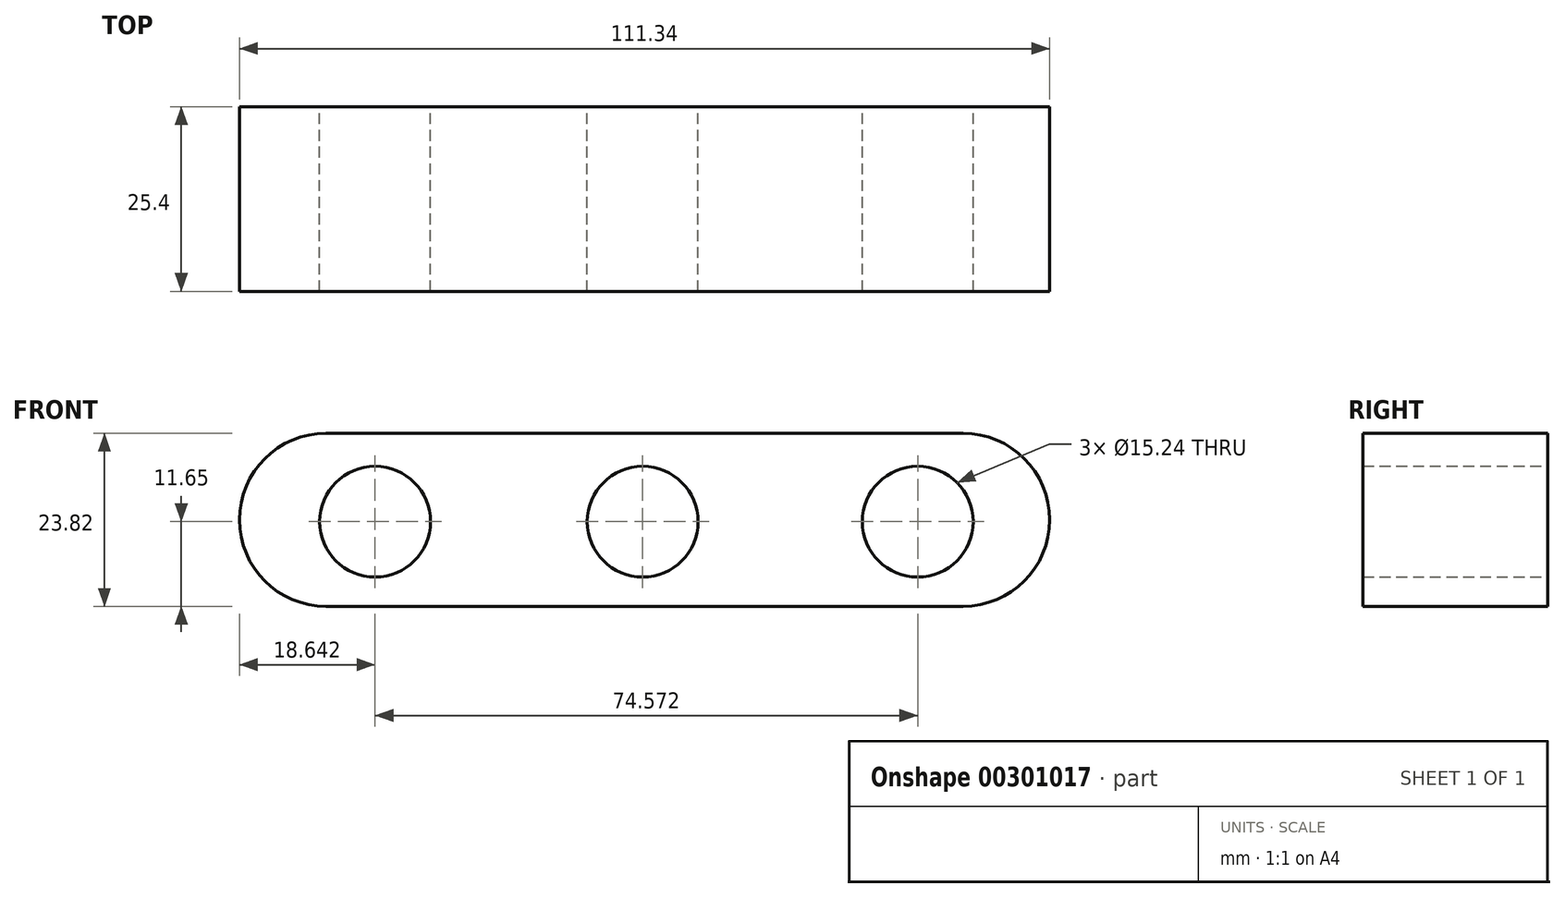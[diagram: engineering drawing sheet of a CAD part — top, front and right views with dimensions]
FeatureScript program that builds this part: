
annotation { "Feature Type Name" : "Feature", "Feature Type Description" : "" }
export const myFeature = defineFeature(function(context is Context, id is Id, definition is map)
    precondition{}
    {
        {
            var Q0;
            Q0=qCreatedBy(makeId("Front.planeOp"),FACE);
            var sketch = newSketch(context, id + "F0", { "sketchPlane" : qUnion([Q0])});
            skLineSegment(sketch, "E0.bottom", {"start": v(-43.5, 12.17) * mm, "end": v(44.02, 12.17) * mm});
            skLineSegment(sketch, "E0.top", {"start": v(-43.5, -11.65) * mm, "end": v(44.02, -11.65) * mm});
            skArc(sketch, "E1", {"start": v(-43.5, 12.17) * mm, "mid": v(-55.41, 0.26) * mm, "end": v(-43.5, -11.65) * mm});
            skArc(sketch, "E2", {"start": v(44.02, -11.65) * mm, "mid": v(55.93, 0.26) * mm, "end": v(44.02, 12.17) * mm});
            skCircle(sketch, "E3", {"center": v(-36.77, 0) * mm, "radius": 9.44 * mm});
            skCircle(sketch, "E4", {"center": v(0, 0) * mm, "radius": 9.44 * mm});
            skCircle(sketch, "E5", {"center": v(37.8, 0) * mm, "radius": 9.44 * mm});
            skSolve(sketch);
        }
        {
            var Q0;
            Q0=makeQuery(id+"F0.imprint","IMPRINT",FACE,{"disambiguationData":[TD([[makeQuery(id+"F0.imprint","IMPRINT",EDGE,{"derivedFrom":sQuery(id+"F0.wireOp",EDGE,"E3")}),1.0]])]});
            var Q1;
            Q1=makeQuery(id+"F0.imprint","IMPRINT",FACE,{"disambiguationData":[TD([[makeQuery(id+"F0.imprint","IMPRINT",EDGE,{"derivedFrom":sQuery(id+"F0.wireOp",EDGE,"E4")}),1.0]])]});
            var Q2;
            Q2=makeQuery(id+"F0.imprint","IMPRINT",FACE,{"disambiguationData":[TD([[makeQuery(id+"F0.imprint","IMPRINT",EDGE,{"derivedFrom":sQuery(id+"F0.wireOp",EDGE,"E5")}),1.0]])]});
            var Q3;
            Q3=makeQuery(id+"F0.imprint","IMPRINT",FACE,{"disambiguationData":[TD([[makeQuery(id+"F0.imprint","IMPRINT",EDGE,{"derivedFrom":sQuery(id+"F0.wireOp",EDGE,"E0.bottom")}),-1.0]])]});
            extrude(context, id + "F1", {"entities" : qUnion([Q0, Q1, Q2, Q3]), "depth" : 25.4 * mm});
        }
        {
            var Q0;
            Q0=sQuery(id+"F0.wireOp",VERTEX,"E3.center");
            var Q1;
            Q1=makeQuery(id+"F1.opExtrude","SWEPT_BODY",BODY,{"disambiguationData":[OSD([sQuery(id+"F0.wireOp",EDGE,"E0.bottom"),sQuery(id+"F0.wireOp",EDGE,"E0.top"),sQuery(id+"F0.wireOp",EDGE,"E1"),sQuery(id+"F0.wireOp",EDGE,"E2")])]});
            hole(context, id + "F2", {"style" : HoleStyle.SIMPLE, "endStyle" : HoleEndStyle.THROUGH, "oppositeDirection" : true, "holeDiameter" : 15.24 * mm, "tappedDepth" : 12.7 * mm, "tapClearance" : 3, "startFromSketch" : true, "locations" : qUnion([Q0]), "scope" : qUnion([Q1])});
        }
        {
            var Q0;
            Q0=sQuery(id+"F0.wireOp",VERTEX,"E4.center");
            var Q1;
            Q1=makeQuery(id+"F1.opExtrude","SWEPT_BODY",BODY,{"disambiguationData":[OSD([sQuery(id+"F0.wireOp",EDGE,"E0.bottom"),sQuery(id+"F0.wireOp",EDGE,"E0.top"),sQuery(id+"F0.wireOp",EDGE,"E1"),sQuery(id+"F0.wireOp",EDGE,"E2")])]});
            hole(context, id + "F3", {"style" : HoleStyle.SIMPLE, "endStyle" : HoleEndStyle.THROUGH, "oppositeDirection" : true, "holeDiameter" : 15.24 * mm, "tappedDepth" : 12.7 * mm, "tapClearance" : 3, "startFromSketch" : true, "locations" : qUnion([Q0]), "scope" : qUnion([Q1])});
        }
        {
            var Q0;
            Q0=sQuery(id+"F0.wireOp",VERTEX,"E5.center");
            var Q1;
            Q1=makeQuery(id+"F1.opExtrude","SWEPT_BODY",BODY,{"disambiguationData":[OSD([sQuery(id+"F0.wireOp",EDGE,"E0.bottom"),sQuery(id+"F0.wireOp",EDGE,"E0.top"),sQuery(id+"F0.wireOp",EDGE,"E1"),sQuery(id+"F0.wireOp",EDGE,"E2")])]});
            hole(context, id + "F4", {"style" : HoleStyle.SIMPLE, "endStyle" : HoleEndStyle.THROUGH, "oppositeDirection" : true, "holeDiameter" : 15.24 * mm, "tappedDepth" : 12.7 * mm, "tapClearance" : 3, "startFromSketch" : true, "locations" : qUnion([Q0]), "scope" : qUnion([Q1])});
        }
    });
